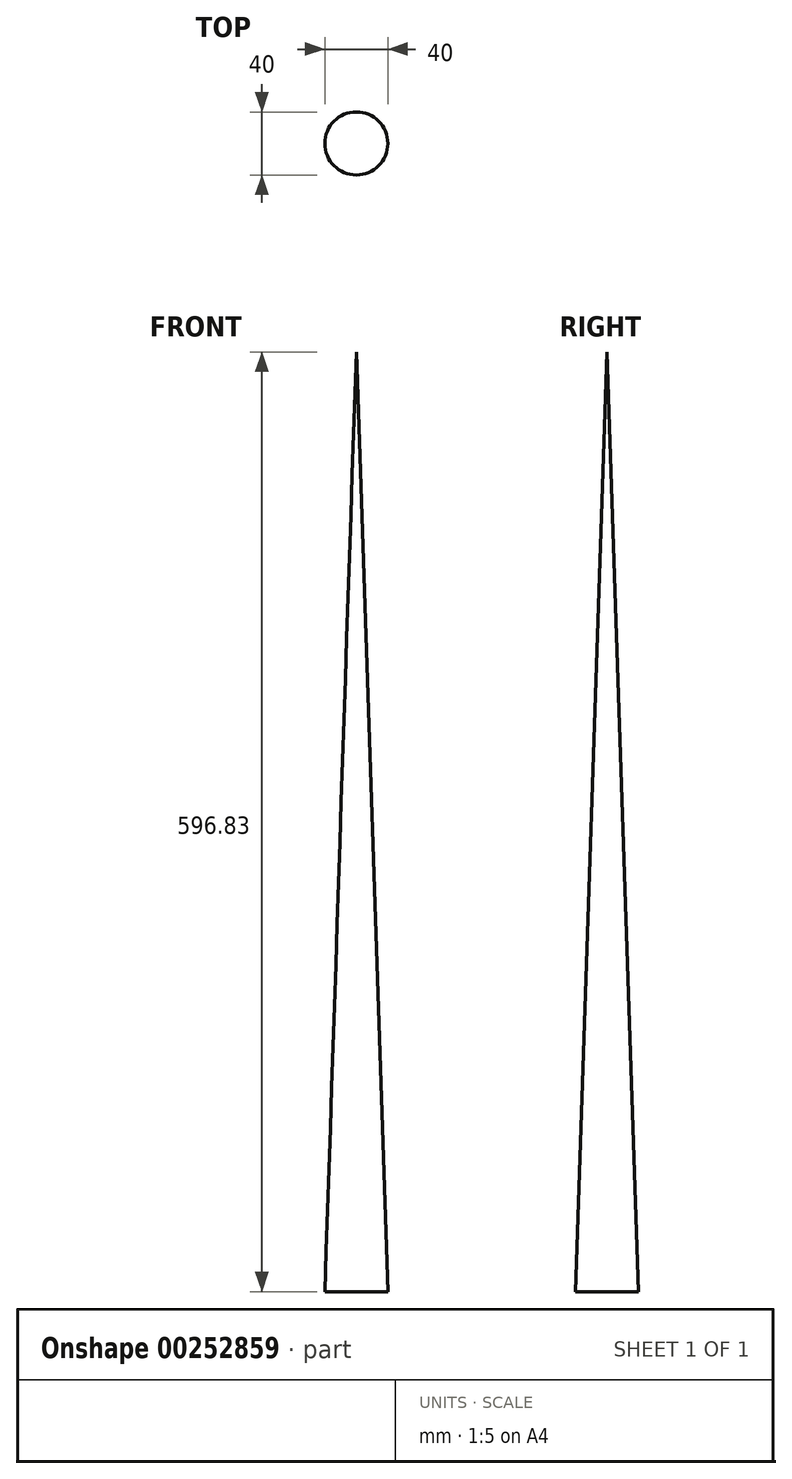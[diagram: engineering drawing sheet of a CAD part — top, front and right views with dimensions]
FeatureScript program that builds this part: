
annotation { "Feature Type Name" : "Feature", "Feature Type Description" : "" }
export const myFeature = defineFeature(function(context is Context, id is Id, definition is map)
    precondition{}
    {
        {
            var Q0;
            Q0=qCreatedBy(makeId("Front.planeOp"),FACE);
            var sketch = newSketch(context, id + "F0", { "sketchPlane" : qUnion([Q0])});
            skLineSegment(sketch, "E0", {"start": v(0, 0) * mm, "end": v(0, 596.83) * mm});
            skLineSegment(sketch, "E1", {"start": v(0, 0) * mm, "end": v(-20, 0) * mm});
            skLineSegment(sketch, "E2", {"start": v(-20, 0) * mm, "end": v(0, 596.83) * mm});
            skSolve(sketch);
        }
        {
            var Q0;
            Q0=makeQuery(id+"F0.imprint","IMPRINT",FACE,{"disambiguationData":[TD([[makeQuery(id+"F0.imprint","IMPRINT",EDGE,{"derivedFrom":sQuery(id+"F0.wireOp",EDGE,"E0")}),1.0]])]});
            var Q1;
            Q1=sQuery(id+"F0.wireOp",EDGE,"E0");
            revolve(context, id + "F1", {"entities" : qUnion([Q0]), "axis" : qUnion([Q1]), "revolveType" : RevolveType.FULL});
        }
    });
